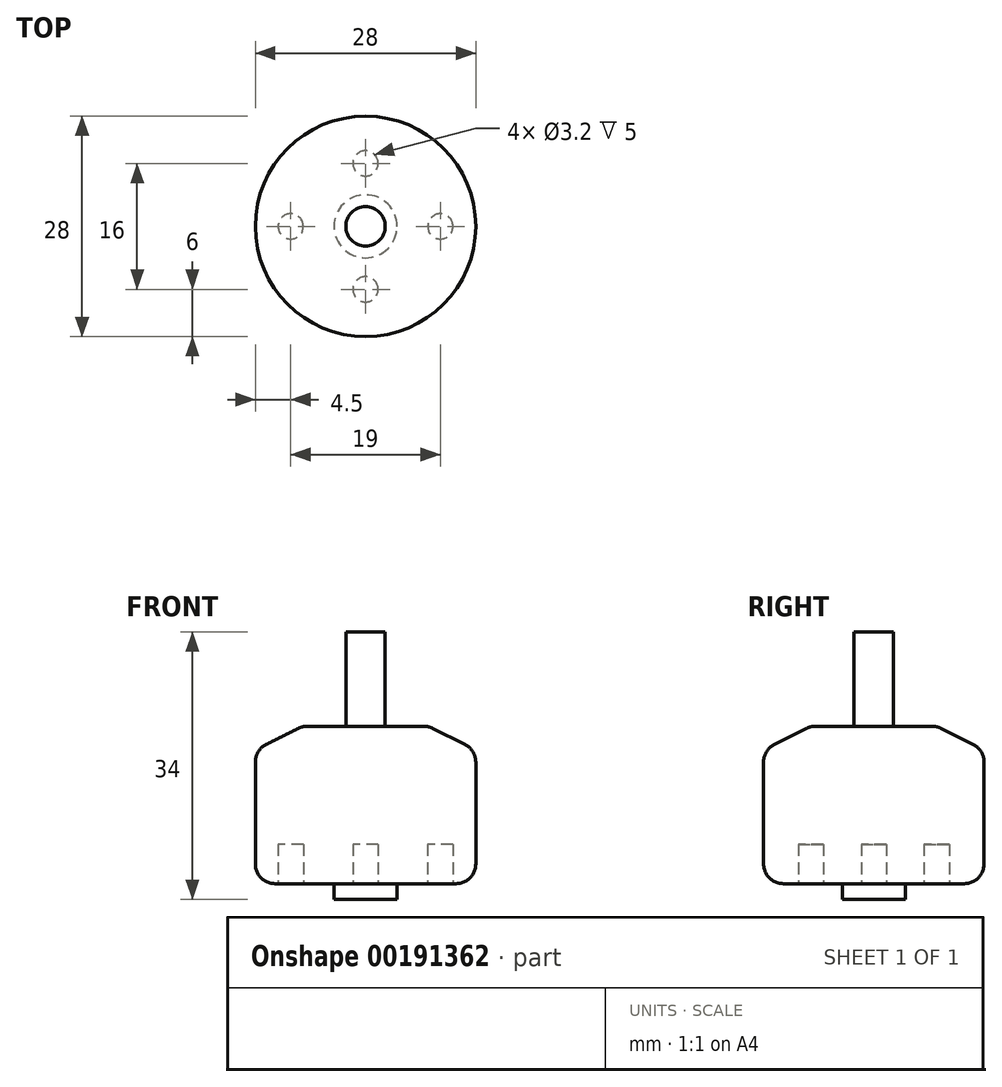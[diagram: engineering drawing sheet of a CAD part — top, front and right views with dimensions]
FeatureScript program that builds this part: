
annotation { "Feature Type Name" : "Feature", "Feature Type Description" : "" }
export const myFeature = defineFeature(function(context is Context, id is Id, definition is map)
    precondition{}
    {
        {
            var Q0;
            Q0=qCreatedBy(makeId("Top.planeOp"),FACE);
            var sketch = newSketch(context, id + "F0", { "sketchPlane" : qUnion([Q0])});
            skCircle(sketch, "E0", {"center": v(0, 0) * mm, "radius": 14 * mm});
            skCircle(sketch, "E1", {"center": v(0, 0) * mm, "radius": 2.5 * mm});
            skCircle(sketch, "E2", {"center": v(0, 0) * mm, "radius": 4 * mm});
            skCircle(sketch, "E3", {"center": v(0, 8) * mm, "radius": 1.6 * mm});
            skCircle(sketch, "E4", {"center": v(-9.5, 0) * mm, "radius": 1.6 * mm});
            skCircle(sketch, "E5", {"center": v(9.5, 0) * mm, "radius": 1.6 * mm});
            skCircle(sketch, "E6", {"center": v(0, -8) * mm, "radius": 1.6 * mm});
            skLineSegment(sketch, "E7", {"start": v(0, 8) * mm, "end": v(0, -8) * mm, "construction": true});
            skLineSegment(sketch, "E8", {"start": v(9.5, 0) * mm, "end": v(-9.5, 0) * mm, "construction": true});
            skSolve(sketch);
        }
        {
            var Q0;
            Q0=makeQuery(id+"F0.imprint","IMPRINT",FACE,{"disambiguationData":[TD([[makeQuery(id+"F0.imprint","IMPRINT",EDGE,{"derivedFrom":sQuery(id+"F0.wireOp",EDGE,"E1")}),-1.0]])]});
            var Q1;
            Q1=makeQuery(id+"F0.imprint","IMPRINT",FACE,{"disambiguationData":[TD([[makeQuery(id+"F0.imprint","IMPRINT",EDGE,{"derivedFrom":sQuery(id+"F0.wireOp",EDGE,"E1")}),1.0]])]});
            var Q2;
            Q2=makeQuery(id+"F0.imprint","IMPRINT",FACE,{"disambiguationData":[TD([[makeQuery(id+"F0.imprint","IMPRINT",EDGE,{"derivedFrom":sQuery(id+"F0.wireOp",EDGE,"E0")}),1.0]])]});
            extrude(context, id + "F1", {"entities" : qUnion([Q0, Q1, Q2]), "depth" : 20 * mm});
        }
        {
            var Q0;
            Q0=makeQuery(id+"F0.imprint","IMPRINT",FACE,{"disambiguationData":[TD([[makeQuery(id+"F0.imprint","IMPRINT",EDGE,{"derivedFrom":sQuery(id+"F0.wireOp",EDGE,"E1")}),1.0]])]});
            extrude(context, id + "F2", {"entities" : qUnion([Q0]), "operationType" : NewBodyOperationType.ADD, "depth" : 32 * mm});
        }
        {
            var Q0;
            Q0=makeQuery(id+"F0.imprint","IMPRINT",FACE,{"disambiguationData":[TD([[makeQuery(id+"F0.imprint","IMPRINT",EDGE,{"derivedFrom":sQuery(id+"F0.wireOp",EDGE,"E1")}),-1.0]])]});
            var Q1;
            Q1=makeQuery(id+"F0.imprint","IMPRINT",FACE,{"disambiguationData":[TD([[makeQuery(id+"F0.imprint","IMPRINT",EDGE,{"derivedFrom":sQuery(id+"F0.wireOp",EDGE,"E1")}),1.0]])]});
            var Q2;
            Q2=sQuery(id+"F0.wireOp",EDGE,"E2");
            extrude(context, id + "F3", {"entities" : qUnion([Q0, Q1]), "operationType" : NewBodyOperationType.ADD, "surfaceEntities" : qUnion([Q2]), "oppositeDirection" : true, "depth" : 2 * mm});
        }
        {
            var Q0;
            Q0=makeQuery(id+"F0.imprint","IMPRINT",FACE,{"disambiguationData":[TD([[makeQuery(id+"F0.imprint","IMPRINT",EDGE,{"derivedFrom":sQuery(id+"F0.wireOp",EDGE,"E3")}),1.0]])]});
            var Q1;
            Q1=makeQuery(id+"F0.imprint","IMPRINT",FACE,{"disambiguationData":[TD([[makeQuery(id+"F0.imprint","IMPRINT",EDGE,{"derivedFrom":sQuery(id+"F0.wireOp",EDGE,"E5")}),1.0]])]});
            var Q2;
            Q2=makeQuery(id+"F0.imprint","IMPRINT",FACE,{"disambiguationData":[TD([[makeQuery(id+"F0.imprint","IMPRINT",EDGE,{"derivedFrom":sQuery(id+"F0.wireOp",EDGE,"E6")}),1.0]])]});
            var Q3;
            Q3=makeQuery(id+"F0.imprint","IMPRINT",FACE,{"disambiguationData":[TD([[makeQuery(id+"F0.imprint","IMPRINT",EDGE,{"derivedFrom":sQuery(id+"F0.wireOp",EDGE,"E4")}),1.0]])]});
            var Q4;
            Q4=makeQuery(id+"F1.opExtrude","CAP_FACE",FACE,{"disambiguationData":[OSD([sQuery(id+"F0.wireOp",EDGE,"E0"),sQuery(id+"F0.wireOp",EDGE,"E3"),sQuery(id+"F0.wireOp",EDGE,"E4"),sQuery(id+"F0.wireOp",EDGE,"E5"),sQuery(id+"F0.wireOp",EDGE,"E6")])],"isStart":false});
            extrude(context, id + "F4", {"entities" : qUnion([Q0, Q1, Q2, Q3]), "operationType" : NewBodyOperationType.ADD, "endBoundEntityFace" : qUnion([Q4]), "depth" : 20 * mm, "hasSecondDirection" : true, "secondDirectionOppositeDirection" : false, "secondDirectionDepth" : 5 * mm});
        }
        {
            var Q0;
            Q0=makeQuery(id+"F1.opExtrude","CAP_EDGE",EDGE,{"disambiguationData":[OSD([sQuery(id+"F0.wireOp",EDGE,"E0")])],"isStart":false});
            chamfer(context, id + "F5", {"entities" : qUnion([Q0]), "chamferType" : ChamferType.TWO_OFFSETS, "width1" : 6 * mm, "oppositeDirection" : false, "width2" : 3 * mm, "tangentPropagation" : true});
        }
        {
            var Q0;
            Q0=makeQuery(id+"F5.opChamfer","BLEND_FACE",FACE,{"disambiguationData":[OSD([sQuery(id+"F0.wireOp",EDGE,"E0")])]});
            var Q1;
            Q1=makeQuery(id+"F1.opExtrude","SWEPT_FACE",FACE,{"disambiguationData":[OSD([sQuery(id+"F0.wireOp",EDGE,"E0")])]});
            fillet(context, id + "F6", {"entities" : qUnion([Q0, Q1]), "radius" : 2.5 * mm, "tangentPropagation" : true, "allowEdgeOverflow" : false});
        }
    });
